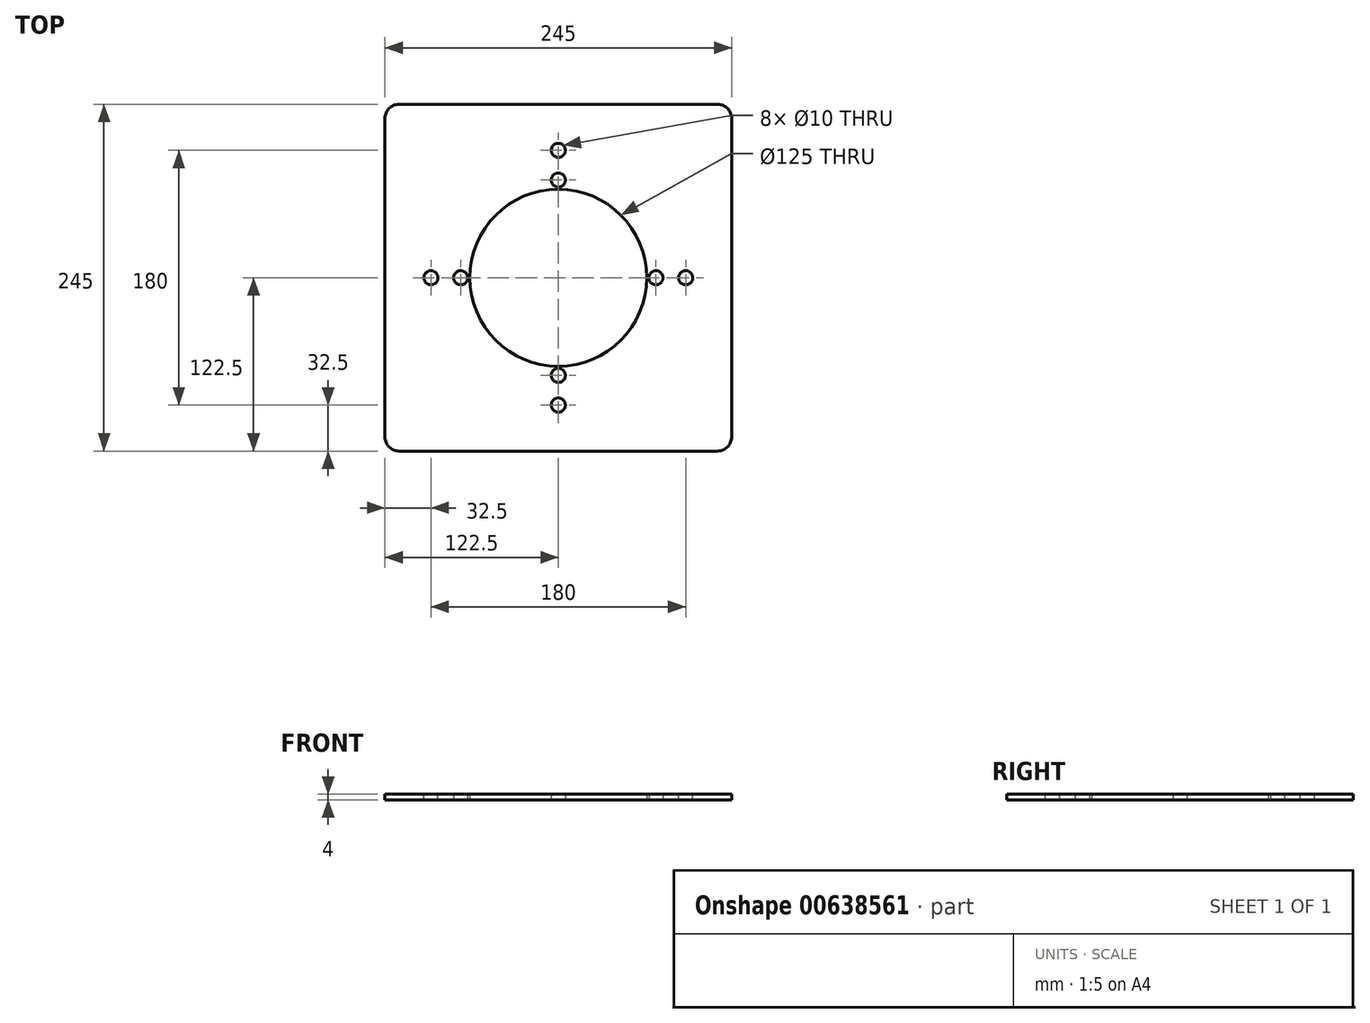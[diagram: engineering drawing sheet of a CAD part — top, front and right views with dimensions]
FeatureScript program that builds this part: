
annotation { "Feature Type Name" : "Feature", "Feature Type Description" : "" }
export const myFeature = defineFeature(function(context is Context, id is Id, definition is map)
    precondition{}
    {
        {
            var Q0;
            Q0=qCreatedBy(makeId("Top.planeOp"),FACE);
            var sketch = newSketch(context, id + "F0", { "sketchPlane" : qUnion([Q0])});
            skLineSegment(sketch, "E0.bottom", {"start": v(-112.5, 122.5) * mm, "end": v(112.5, 122.5) * mm});
            skLineSegment(sketch, "E0.top", {"start": v(-112.5, -122.5) * mm, "end": v(112.5, -122.5) * mm});
            skLineSegment(sketch, "E0.left", {"start": v(-122.5, 112.5) * mm, "end": v(-122.5, -112.5) * mm});
            skLineSegment(sketch, "E0.right", {"start": v(122.5, 112.5) * mm, "end": v(122.5, -112.5) * mm});
            skPoint(sketch, "E0.middle", {"position": v(0, 0) * mm});
            skCircle(sketch, "E1", {"center": v(0, 0) * mm, "radius": 62.5 * mm});
            skCircle(sketch, "E2", {"center": v(0, 0) * mm, "radius": 69 * mm, "construction": true});
            skCircle(sketch, "E3", {"center": v(0, 69) * mm, "radius": 5 * mm});
            skCircle(sketch, "E4.1.0", {"center": v(-69, 0) * mm, "radius": 5 * mm});
            skCircle(sketch, "E4.2.0", {"center": v(0, -69) * mm, "radius": 5 * mm});
            skCircle(sketch, "E4.3.0", {"center": v(69, 0) * mm, "radius": 5 * mm});
            skPoint(sketch, "E5.visualSharp", {"position": v(-122.5, 122.5) * mm});
            skArc(sketch, "E5.filletArc", {"start": v(-112.5, 122.5) * mm, "mid": v(-119.57, 119.57) * mm, "end": v(-122.5, 112.5) * mm});
            skPoint(sketch, "E6.visualSharp", {"position": v(122.5, 122.5) * mm});
            skArc(sketch, "E6.filletArc", {"start": v(122.5, 112.5) * mm, "mid": v(119.57, 119.57) * mm, "end": v(112.5, 122.5) * mm});
            skPoint(sketch, "E7.visualSharp", {"position": v(122.5, -122.5) * mm});
            skArc(sketch, "E7.filletArc", {"start": v(112.5, -122.5) * mm, "mid": v(119.57, -119.57) * mm, "end": v(122.5, -112.5) * mm});
            skPoint(sketch, "E8.visualSharp", {"position": v(-122.5, -122.5) * mm});
            skArc(sketch, "E8.filletArc", {"start": v(-122.5, -112.5) * mm, "mid": v(-119.57, -119.57) * mm, "end": v(-112.5, -122.5) * mm});
            skSolve(sketch);
        }
        {
            var Q0;
            Q0=qSketchRegion(id+"F0",true);
            extrude(context, id + "F1", {"entities" : qUnion([Q0]), "depth" : 4 * mm, "offsetDistance" : 25 * mm});
        }
        {
            var Q0;
            Q0=makeQuery(id+"F1.opExtrude","CAP_FACE",FACE,{"disambiguationData":[OSD([sQuery(id+"F0.wireOp",EDGE,"E0.bottom"),sQuery(id+"F0.wireOp",EDGE,"E0.top"),sQuery(id+"F0.wireOp",EDGE,"E0.left"),sQuery(id+"F0.wireOp",EDGE,"E0.right"),sQuery(id+"F0.wireOp",EDGE,"E1"),sQuery(id+"F0.wireOp",EDGE,"E3"),sQuery(id+"F0.wireOp",EDGE,"E4.1.0"),sQuery(id+"F0.wireOp",EDGE,"E4.2.0"),sQuery(id+"F0.wireOp",EDGE,"E4.3.0"),sQuery(id+"F0.wireOp",EDGE,"E5.filletArc"),sQuery(id+"F0.wireOp",EDGE,"E6.filletArc"),sQuery(id+"F0.wireOp",EDGE,"E7.filletArc"),sQuery(id+"F0.wireOp",EDGE,"E8.filletArc")])],"isStart":false});
            var sketch = newSketch(context, id + "F2", { "sketchPlane" : qUnion([Q0])});
            skCircle(sketch, "E9", {"center": v(0, 0) * mm, "radius": 90 * mm, "construction": true});
            skCircle(sketch, "E10", {"center": v(0, 90) * mm, "radius": 5 * mm});
            skCircle(sketch, "E11.1.0", {"center": v(-90, 0) * mm, "radius": 5 * mm});
            skCircle(sketch, "E11.2.0", {"center": v(0, -90) * mm, "radius": 5 * mm});
            skCircle(sketch, "E11.3.0", {"center": v(90, 0) * mm, "radius": 5 * mm});
            skSolve(sketch);
        }
        {
            var Q0;
            Q0 = qSketchRegion(id + "F2", true);
            extrude(context, id + "F3", {"entities" : qUnion([Q0]), "operationType" : NewBodyOperationType.REMOVE, "oppositeDirection" : true, "depth" : 25 * mm, "offsetDistance" : 25 * mm});
        }
    });
